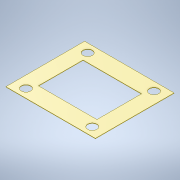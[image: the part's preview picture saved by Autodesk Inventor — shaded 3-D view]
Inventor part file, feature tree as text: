
AUTODESK INVENTOR PART (.ipt)
format: ipt  version: 2020 (Build 240168000, 168)  size: 123,392 bytes
history: native  units: mm
features: extrude x3, sketch x3
ambient origin geometry x8: Origin, YZ Plane, XZ Plane, XY Plane, X Axis, Y Axis, Z Axis, Center Point
bodies: Solid1 (feature_tree)
feature tree (6):
  extrude  "Extrusion1"  Depth=25.5mm
  extrude  "Extrusion2"  Depth=0.13mm
  extrude  "Extrusion3"  Depth=14.5mm
  sketch  "Sketch1"  dims[d0=29.0mm d1=25.5mm]
  sketch  "Sketch2"  dims[d2=0.13mm d3=0.0mm d4=3.0mm]
  sketch  "Sketch3"  dims[d5=2.75mm d6=3.75mm d7=20.0mm d9=21.5mm d10=20.0mm d12=20.0mm d15=0.0mm d16=0.0mm d17=19.0mm d18=14.5mm d19=0.0mm d20=0.0mm]
